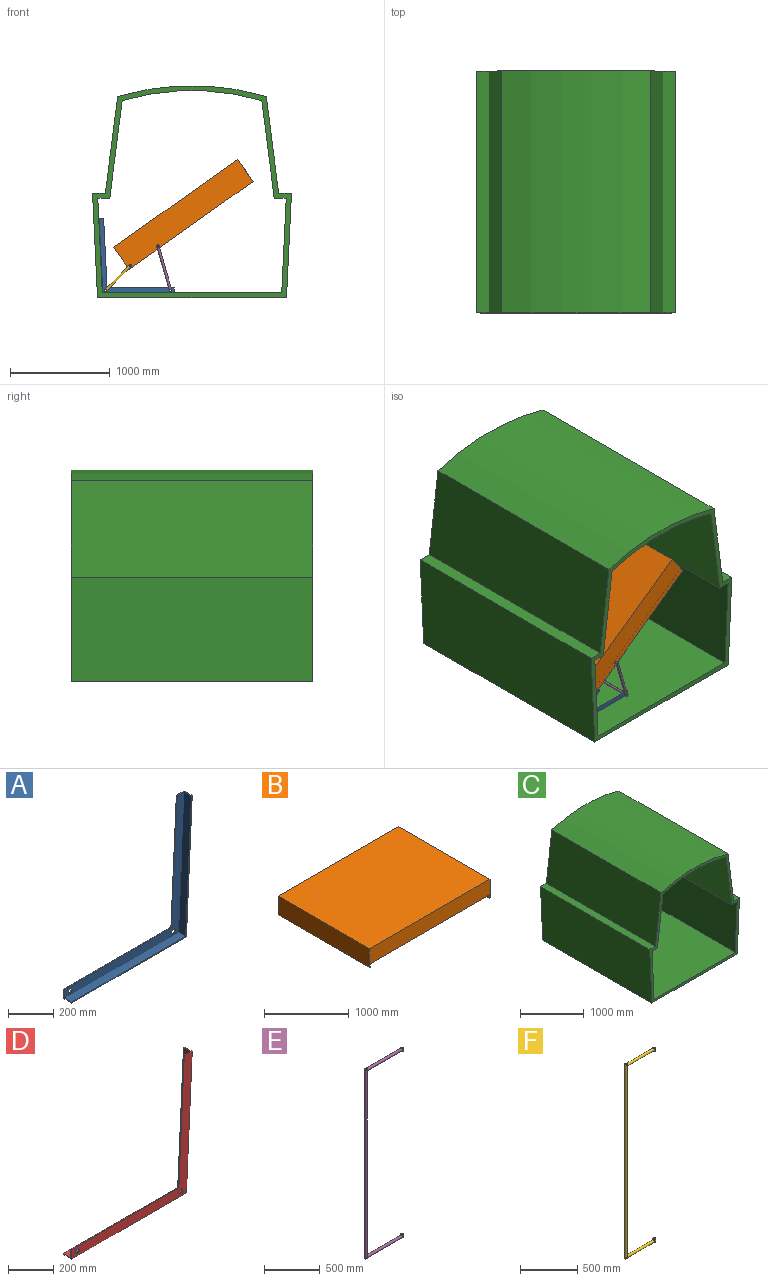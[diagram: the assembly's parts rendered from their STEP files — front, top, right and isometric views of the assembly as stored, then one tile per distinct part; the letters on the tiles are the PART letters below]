
ASSEMBLY  parts=6 mates=7
PART A: 13 faces, bbox 756.5x50x751.5 mm
  f0: plane 50x49.94mm, normal (0.05,0,1), area 475mm2, adj f2,f3,f4,f7,f8,f10
  f1: plane 50x50mm, normal (-1,0,0), area 475mm2, adj f5,f6,f7,f8,f9,f10
  f2: plane 701.54x34.19mm, normal (-1,0,0.05), area 3511.9mm2, adj f0,f6,f7,f10
  f3: plane 749.11x50mm, normal (1,0,-0.05), area 37500mm2, adj f0,f5,f7,f8
  f4: plane 744.35x45mm, normal (-1,0,0.05), area 33535.7mm2, adj f0,f8,f9,f10
  f5: plane 720x50mm, normal (0,0,-1), area 36000mm2, adj f1,f3,f7,f8
  f6: plane 672.38x5mm, normal (0,0,1), area 3361.9mm2, adj f1,f2,f7,f10
  f7: plane 756.51x751.54mm, normal (0,1,0), area 70137.1mm2, adj f0,f1,f2,f3,f5,f6,f11,f12
  f8: plane 756.51x749.35mm, normal (0,-1,0), area 7326.2mm2, adj f0,f1,f3,f4,f5,f9
  f9: plane 715.24x45mm, normal (0,0,1), area 32185.7mm2, adj f1,f4,f8,f10
  f10: plane 751.51x746.54mm, normal (0,-1,0), area 62810.9mm2, adj f0,f1,f2,f4,f6,f9,f11,f12
  f11: cylinder r=12.5mm len=25mm, axis (0,1,0), area 392.7mm2, adj f7,f10
  f12: cylinder r=12.5mm len=25mm, axis (0,1,0), area 392.7mm2, adj f7,f10
PART B: 14 faces, bbox 2010x1524x270 mm
  f0: plane 1990x1524mm, normal (0,0,-1), area 3032760mm2, adj f1,f3,f5,f9
  f1: plane 2010x270mm, normal (0,-1,0), area 443200mm2, adj f0,f2,f4,f5,f6,f7,f8,f9
  f2: plane 1524x270mm, normal (1,0,0), area 411253.8mm2, adj f1,f3,f4,f6,f11,f13
  f3: plane 2010x270mm, normal (0,1,0), area 443200mm2, adj f0,f2,f4,f5,f6,f7,f8,f9
  f4: plane 2010x1524mm, normal (0,0,1), area 3063240mm2, adj f1,f2,f3,f8
  f5: plane 1524x50mm, normal (-1,0,0), area 75973.8mm2, adj f0,f1,f3,f6,f11,f13
  f6: plane 1524x10mm, normal (0,0,-1), area 15240mm2, adj f1,f2,f3,f5
  f7: plane 1524x10mm, normal (0,0,-1), area 15240mm2, adj f1,f3,f8,f9
  f8: plane 1524x270mm, normal (-1,0,0), area 411253.8mm2, adj f1,f3,f4,f7,f10,f12
  f9: plane 1524x50mm, normal (1,0,0), area 75973.8mm2, adj f0,f1,f3,f7,f10,f12
  f10: cylinder r=6mm len=12mm, axis (1,0,0), area 377mm2, adj f8,f9
  f11: cylinder r=6mm len=12mm, axis (1,0,0), area 377mm2, adj f2,f5
  f12: cylinder r=6mm len=12mm, axis (1,0,0), area 377mm2, adj f8,f9
  f13: cylinder r=6mm len=12mm, axis (1,0,0), area 377mm2, adj f2,f5
PART C: 18 faces, bbox 1994.8x2425x2130 mm
  f0: plane 2425x950.94mm, normal (1,0,0.05), area 2308600mm2, adj f1,f15,f16,f17
  f1: plane 2425x120mm, normal (0,0,-1), area 291000mm2, adj f0,f2,f16,f17
  f2: plane 2425x979.05mm, normal (0.99,0,-0.13), area 2393475mm2, adj f1,f3,f16,f17
  f3: cylinder r=2500mm len=2425mm, axis (0,1,0), area 3441003.6mm2, adj f2,f4,f16,f17
  f4: plane 2425x979.05mm, normal (-0.99,0,-0.13), area 2393475mm2, adj f3,f5,f16,f17
  f5: plane 2425x120mm, normal (0,0,-1), area 291000mm2, adj f4,f6,f16,f17
  f6: plane 2425x950.94mm, normal (-1,0,0.05), area 2308600mm2, adj f5,f15,f16,f17
  f7: plane 2425x1050.94mm, normal (-1,0,-0.05), area 2551371.4mm2, adj f8,f14,f16,f17
  f8: plane 2425x1895.38mm, normal (0,0,-1), area 4596295.8mm2, adj f7,f9,f16,f17
  f9: plane 2425x1050.94mm, normal (1,0,-0.05), area 2551371.4mm2, adj f8,f10,f16,f17
  f10: plane 2425x128.4mm, normal (0,0,1), area 311369.7mm2, adj f9,f11,f16,f17
  f11: plane 2425x968.28mm, normal (0.99,0,0.13), area 2367149.4mm2, adj f10,f12,f16,f17
  f12: cylinder r=2563.39mm len=2425mm, axis (0,1,0), area 3668165.1mm2, adj f11,f13,f16,f17
  f13: plane 2425x968.28mm, normal (-0.99,0,0.13), area 2367149.4mm2, adj f12,f14,f16,f17
  f14: plane 2425x128.4mm, normal (0,0,1), area 311369.7mm2, adj f7,f13,f16,f17
  f15: plane 2425x1800mm, normal (0,0,1), area 4365000mm2, adj f0,f6,f16,f17
  f16: plane 2129.99x1994.84mm, normal (0,-1,0), area 376732.6mm2, adj f0,f1,f2,f3,f4,f5,f6,f7
  f17: plane 2129.99x1994.84mm, normal (0,1,0), area 376732.6mm2, adj f0,f1,f2,f3,f4,f5,f6,f7
PART D: 13 faces, bbox 756.5x50x751.5 mm
  f0: plane 50x49.94mm, normal (0.05,0,1), area 475mm2, adj f2,f3,f4,f7,f8,f10
  f1: plane 50x50mm, normal (-1,0,0), area 475mm2, adj f5,f6,f7,f8,f9,f10
  f2: plane 701.54x34.19mm, normal (-1,0,0.05), area 3511.9mm2, adj f0,f6,f7,f10
  f3: plane 749.11x50mm, normal (1,0,-0.05), area 37500mm2, adj f0,f5,f7,f8
  f4: plane 744.35x45mm, normal (-1,0,0.05), area 33535.7mm2, adj f0,f8,f9,f10
  f5: plane 720x50mm, normal (0,0,-1), area 36000mm2, adj f1,f3,f7,f8
  f6: plane 672.38x5mm, normal (0,0,1), area 3361.9mm2, adj f1,f2,f7,f10
  f7: plane 756.51x751.54mm, normal (0,-1,0), area 70137.1mm2, adj f0,f1,f2,f3,f5,f6,f11,f12
  f8: plane 756.51x749.35mm, normal (0,1,0), area 7326.2mm2, adj f0,f1,f3,f4,f5,f9
  f9: plane 715.24x45mm, normal (0,0,1), area 32185.7mm2, adj f1,f4,f8,f10
  f10: plane 751.51x746.54mm, normal (0,1,0), area 62810.9mm2, adj f0,f1,f2,f4,f6,f9,f11,f12
  f11: cylinder r=12.5mm len=25mm, axis (0,-1,0), area 392.7mm2, adj f7,f10
  f12: cylinder r=12.5mm len=25mm, axis (0,-1,0), area 392.7mm2, adj f7,f10
PART E: 16 faces, bbox 490x25x2080 mm
  f0: cylinder r=12.5mm len=12.5mm, axis (0,0,-1), area 89.2mm2, adj f1,f3,f4
  f1: cylinder r=12.5mm len=2080mm, axis (0,0,-1), area 161934.4mm2, adj f0,f2,f3,f4,f10,f11
  f2: cylinder r=12.5mm len=12.5mm, axis (0,0,-1), area 89.2mm2, adj f1,f10,f11
  f3: plane 25x25mm, normal (0,0,-1), area 176.7mm2, adj f0,f1,f9
  f4: cylinder r=12.5mm len=465mm, axis (-1,0,0), area 35271mm2, adj f0,f1,f5
  f5: cylinder r=12.5mm len=35mm, axis (0,0,-1), area 2123.9mm2, adj f4,f6,f7
  f6: plane 25x25mm, normal (0,0,1), area 176.7mm2, adj f5,f8
  f7: plane 25x25mm, normal (0,0,-1), area 176.7mm2, adj f5,f8
  f8: cylinder r=10mm len=35mm, axis (0,0,1), area 2199.1mm2, adj f6,f7
  f9: cylinder r=10mm len=2080mm, axis (0,0,1), area 130690.3mm2, adj f3,f10
  f10: plane 25x25mm, normal (0,0,1), area 176.7mm2, adj f1,f2,f9
  f11: cylinder r=12.5mm len=465mm, axis (-1,0,0), area 35271mm2, adj f1,f2,f12
  f12: cylinder r=12.5mm len=35mm, axis (0,0,1), area 2123.9mm2, adj f11,f13,f14
  f13: plane 25x25mm, normal (0,0,-1), area 176.7mm2, adj f12,f15
  f14: plane 25x25mm, normal (0,0,1), area 176.7mm2, adj f12,f15
  f15: cylinder r=10mm len=35mm, axis (0,0,-1), area 2199.1mm2, adj f13,f14
PART F: 16 faces, bbox 375x25x2080 mm
  f0: cylinder r=12.5mm len=12.5mm, axis (0,0,-1), area 89.2mm2, adj f1,f3,f4
  f1: cylinder r=12.5mm len=2080mm, axis (0,0,-1), area 161934.4mm2, adj f0,f2,f3,f4,f10,f11
  f2: cylinder r=12.5mm len=12.5mm, axis (0,0,-1), area 89.2mm2, adj f1,f10,f11
  f3: plane 25x25mm, normal (0,0,-1), area 176.7mm2, adj f0,f1,f9
  f4: cylinder r=12.5mm len=350mm, axis (-1,0,0), area 26238.9mm2, adj f0,f1,f5
  f5: cylinder r=12.5mm len=35mm, axis (0,0,-1), area 2123.9mm2, adj f4,f6,f7
  f6: plane 25x25mm, normal (0,0,1), area 176.7mm2, adj f5,f8
  f7: plane 25x25mm, normal (0,0,-1), area 176.7mm2, adj f5,f8
  f8: cylinder r=10mm len=35mm, axis (0,0,1), area 2199.1mm2, adj f6,f7
  f9: cylinder r=10mm len=2080mm, axis (0,0,1), area 130690.3mm2, adj f3,f10
  f10: plane 25x25mm, normal (0,0,1), area 176.7mm2, adj f1,f2,f9
  f11: cylinder r=12.5mm len=350mm, axis (-1,0,0), area 26238.9mm2, adj f1,f2,f12
  f12: cylinder r=12.5mm len=35mm, axis (0,0,1), area 2123.9mm2, adj f11,f13,f14
  f13: plane 25x25mm, normal (0,0,-1), area 176.7mm2, adj f12,f15
  f14: plane 25x25mm, normal (0,0,1), area 176.7mm2, adj f12,f15
  f15: cylinder r=10mm len=35mm, axis (0,0,-1), area 2199.1mm2, adj f13,f14
PLACE A rot(axis=(0,0,1),180deg) t=(-194.95,-2013.56,-270.86)mm fixed
PLACE B rot(axis=(0.29,-0.29,-0.91),95.3deg) t=(-674.31,-1903.56,7.55)mm
PLACE C t=(-15.34,213.79,-270.86)mm fixed
PLACE D rot(axis=(0,0,-1),180deg) t=(-194.95,216.44,-270.86)mm
PLACE E rot(axis=(0.47,-0.62,0.62),129.6deg) t=(-229.95,141.44,-245.86)mm
PLACE F rot(axis=(-0.86,-0.36,-0.36),98.6deg) t=(-879.95,-1938.56,-245.86)mm
MATE revolute E.f0 <-> A.f12  axis (0,-1,0) through (-229.95,-1938.56,-245.86)mm
MATE revolute D.f12 <-> E.f0  axis (0,1,0) through (-229.95,116.44,-245.86)mm
MATE planar C.f15 <-> D.f5  axis (0,0,1) through (-15.34,-998.71,-270.86)mm
MATE planar A.f5 <-> C.f15  axis (0,0,-1) through (-554.95,-1888.56,-270.86)mm
MATE revolute B.f10 <-> F.f8  axis (0,-1,0) through (-635.38,-1903.56,4.51)mm
MATE revolute D.f11 <-> F.f0  axis (0,1,0) through (-879.95,116.44,-245.86)mm
MATE cylindrical B.f12 <-> E.f5  axis (0,-1,0) through (-358.02,-1903.56,201.16)mm
